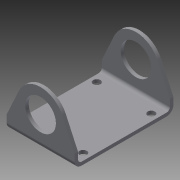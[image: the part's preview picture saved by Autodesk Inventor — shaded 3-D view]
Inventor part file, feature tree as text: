
AUTODESK INVENTOR PART (.ipt)
format: ipt  version: 2013 (Build 170138000, 138)  size: 161,792 bytes
history: native  units: in
note: dims shown in document units (in); Inventor stores cm internally (conversion verified against a paired STEP export)
features: sheet_metal_op x4, sketch x4, other x4
ambient origin geometry x8: Origin, YZ Plane, XZ Plane, XY Plane, X Axis, Y Axis, Z Axis, Center Point
bodies: Solid1 (feature_tree)
feature tree (12):
  sheet_metal_op  "Face1"
  sheet_metal_op  "Flange1"
  sketch  "Sketch1"  dims[d0=3.626in]
  other  "Plate1"
  sketch  "Sketch2"  dims[d2=2.5in]
  other  "Plate2"
  sheet_metal_op  "Bend1"
  sheet_metal_op  "Corner1"
  sketch  "Sketch3"  dims[d3=0.125in]
  sketch  "Sketch4"  dims[d4=0.125in d5=0.0625in d6=0.25in d7=0.125in d8=2.0in d9=90.0deg d10=0.125in d11=0.5in d12=0.125in d13=0.125in d14=1.125in d15=0.25in d16=1.125in d17=1.75in d18=1.25in d19=0.25in d20=100.0in d21=0.0in d22=0.266in d23=0.266in d24=0.266in d25=0.266in d26=1.25in d27=1.25in d28=1.25in d29=1.25in d30=0.25in d31=0.25in d32=0.25in d33=0.25in d34=0.125in d35=0.0in]
  other  "Cut1"
  other  "Cut2"
